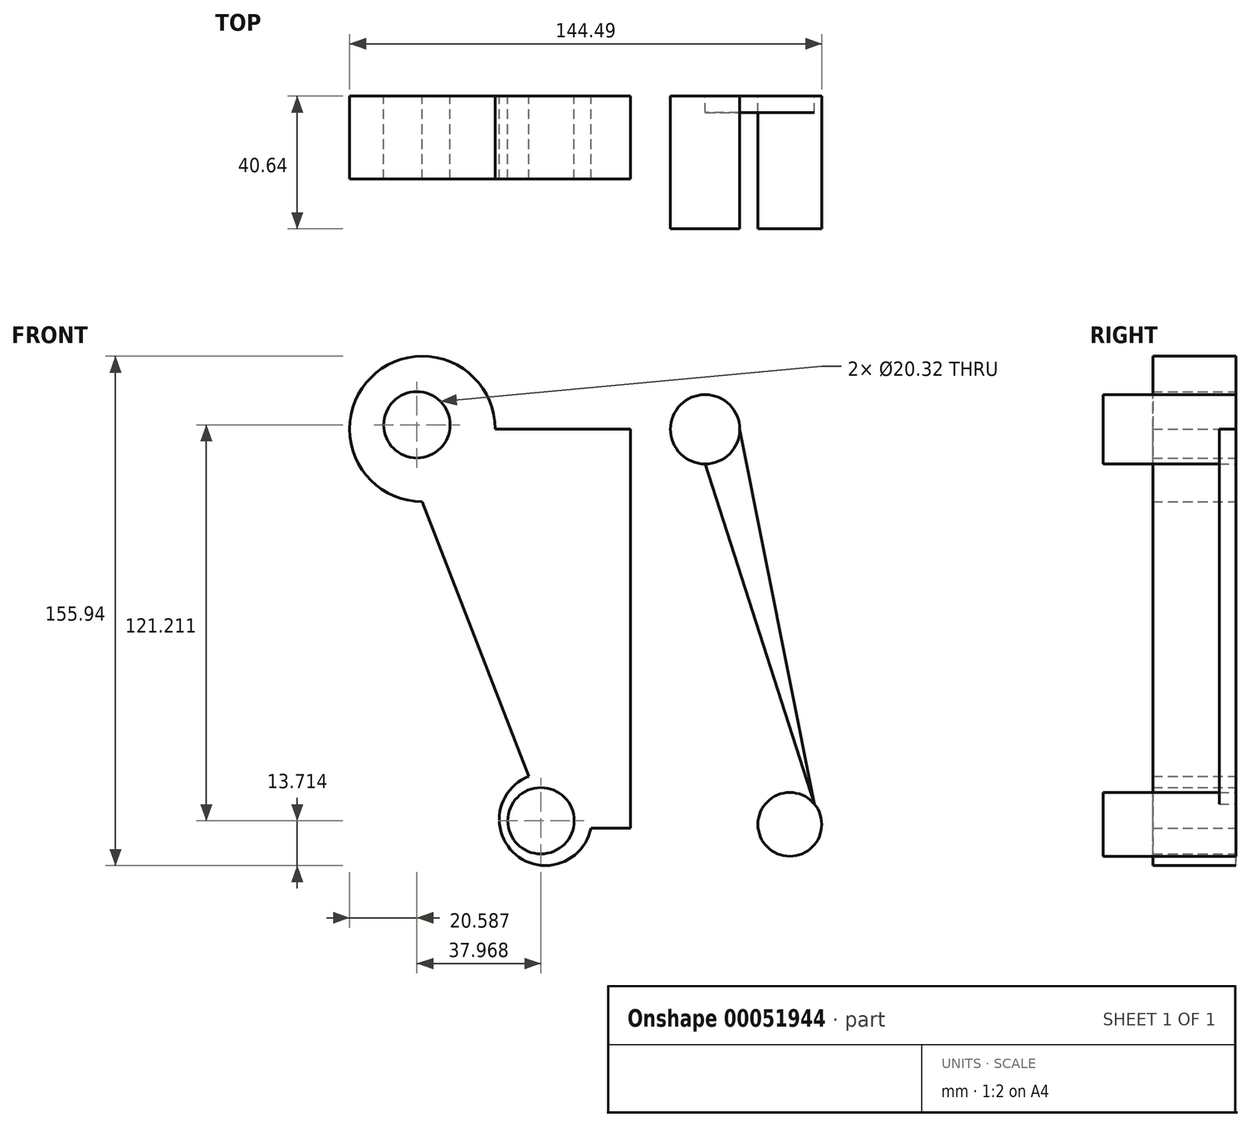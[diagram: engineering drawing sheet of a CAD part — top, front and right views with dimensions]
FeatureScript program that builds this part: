
annotation { "Feature Type Name" : "Feature", "Feature Type Description" : "" }
export const myFeature = defineFeature(function(context is Context, id is Id, definition is map)
    precondition{}
    {
        {
            var Q0;
            Q0=qCreatedBy(makeId("Front.planeOp"),FACE);
            var sketch = newSketch(context, id + "F0", { "sketchPlane" : qUnion([Q0])});
            skLineSegment(sketch, "E0", {"start": v(0, 44.6) * mm, "end": v(-63.66, 44.6) * mm});
            skCircle(sketch, "E1", {"center": v(-63.66, 44.6) * mm, "radius": 22.27 * mm});
            skLineSegment(sketch, "E2", {"start": v(-63.66, 22.34) * mm, "end": v(-25.98, -74.92) * mm});
            skCircle(sketch, "E3", {"center": v(-25.98, -74.92) * mm, "radius": 14.14 * mm});
            skLineSegment(sketch, "E4", {"start": v(-12.1, -77.57) * mm, "end": v(0, -77.57) * mm});
            skLineSegment(sketch, "E5", {"start": v(0, -77.57) * mm, "end": v(0, 44.6) * mm});
            skLineSegment(sketch, "E6", {"start": v(0, 90.08) * mm, "end": v(0, -110.43) * mm});
            skSolve(sketch);
        }
        {
            var Q0;
            {var subQ0=sQuery(id+"F0.wireOp",EDGE,"E3");var subQ1=makeQuery(id+"F0.imprint","INTERSECT",VERTEX,{"derivedFrom":[subQ0,sQuery(id+"F0.wireOp",EDGE,"E4")]});Q0=makeQuery(id+"F0.imprint","IMPRINT",FACE,{"disambiguationData":[TD([[makeQuery(id+"F0.imprint","IMPRINT",EDGE,{"disambiguationData":[TD([[subQ1,1.0]])],"derivedFrom":subQ0}),1.0]])]});}
            var Q1;
            {var subQ0=sQuery(id+"F0.wireOp",EDGE,"E1");var subQ1=makeQuery(id+"F0.imprint","INTERSECT",VERTEX,{"derivedFrom":[subQ0,sQuery(id+"F0.wireOp",EDGE,"E2")]});Q1=makeQuery(id+"F0.imprint","IMPRINT",FACE,{"disambiguationData":[TD([[makeQuery(id+"F0.imprint","IMPRINT",EDGE,{"disambiguationData":[TD([[subQ1,1.0]])],"derivedFrom":subQ0}),1.0]])]});}
            var Q2;
            {var subQ0=sQuery(id+"F0.wireOp",EDGE,"E4");Q2=makeQuery(id+"F0.imprint","IMPRINT",FACE,{"disambiguationData":[TD([[makeQuery(id+"F0.imprint","IMPRINT",EDGE,{"derivedFrom":subQ0}),1.0]])]});}
            extrude(context, id + "F1", {"entities" : qUnion([Q0, Q1, Q2]), "depth" : 25.4 * mm});
        }
        {
            var Q0;
            Q0=qCreatedBy(makeId("Front.planeOp"),FACE);
            var sketch = newSketch(context, id + "F2", { "sketchPlane" : qUnion([Q0])});
            skCircle(sketch, "E7", {"center": v(-65.34, 45.87) * mm, "radius": 15.9 * mm});
            skCircle(sketch, "E8", {"center": v(-27.38, -75.35) * mm, "radius": 8.7 * mm});
            skSolve(sketch);
        }
        {
            var Q0;
            Q0=sQuery(id+"F2.wireOp",VERTEX,"E7.center");
            var Q1;
            Q1=sQuery(id+"F2.wireOp",VERTEX,"E8.center");
            var Q2;
            Q2=makeQuery(id+"F1.opExtrude","SWEPT_BODY",BODY,{"disambiguationData":[OSD([sQuery(id+"F0.wireOp",EDGE,"E0"),sQuery(id+"F0.wireOp",EDGE,"E1"),sQuery(id+"F0.wireOp",EDGE,"E2"),sQuery(id+"F0.wireOp",EDGE,"E3"),sQuery(id+"F0.wireOp",EDGE,"E4"),sQuery(id+"F0.wireOp",EDGE,"E6")])]});
            hole(context, id + "F3", {"style" : HoleStyle.SIMPLE, "holeDiameter" : 20.32 * mm, "endStyle" : HoleEndStyle.THROUGH, "oppositeDirection" : true, "locations" : qUnion([Q0, Q1]), "scope" : qUnion([Q2])});
        }
        {
            var Q0;
            Q0=qCreatedBy(makeId("Front.planeOp"),FACE);
            var sketch = newSketch(context, id + "F4", { "sketchPlane" : qUnion([Q0])});
            skCircle(sketch, "E9", {"center": v(48.8, -76.46) * mm, "radius": 9.76 * mm});
            skSolve(sketch);
        }
        {
            var Q0;
            Q0=qCreatedBy(makeId("Front.planeOp"),FACE);
            var sketch = newSketch(context, id + "F5", { "sketchPlane" : qUnion([Q0])});
            skCircle(sketch, "E10", {"center": v(22.87, 44.5) * mm, "radius": 10.62 * mm});
            skLineSegment(sketch, "E11", {"start": v(30.6, 49.5) * mm, "end": v(33.49, 44.5) * mm});
            skLineSegment(sketch, "E12", {"start": v(33.49, 44.5) * mm, "end": v(56.27, -70.25) * mm});
            skLineSegment(sketch, "E13", {"start": v(56.27, -70.25) * mm, "end": v(22.87, 33.89) * mm});
            skSolve(sketch);
        }
        {
            var Q0;
            {var subQ0=sQuery(id+"F5.wireOp",EDGE,"E10");var subQ1=makeQuery(id+"F5.imprint","INTERSECT",VERTEX,{"derivedFrom":[subQ0,sQuery(id+"F5.wireOp",EDGE,"E12")]});Q0=makeQuery(id+"F5.imprint","IMPRINT",FACE,{"disambiguationData":[TD([[makeQuery(id+"F5.imprint","IMPRINT",EDGE,{"disambiguationData":[TD([[subQ1,-1.0]])],"derivedFrom":subQ0}),1.0]])]});}
            var Q1;
            Q1=makeQuery(id+"F4.imprint","IMPRINT",FACE,{"disambiguationData":[TD([[makeQuery(id+"F4.imprint","IMPRINT",EDGE,{"derivedFrom":sQuery(id+"F4.wireOp",EDGE,"E9")}),1.0]])]});
            extrude(context, id + "F6", {"entities" : qUnion([Q0, Q1]), "depth" : 40.64 * mm});
        }
        {
            var Q0;
            {var subQ0=sQuery(id+"F5.wireOp",EDGE,"E12");Q0=makeQuery(id+"F5.imprint","IMPRINT",FACE,{"disambiguationData":[TD([[makeQuery(id+"F5.imprint","IMPRINT",EDGE,{"derivedFrom":subQ0}),-1.0]])]});}
            extrude(context, id + "F7", {"entities" : qUnion([Q0]), "depth" : 5.08 * mm});
        }
    });
